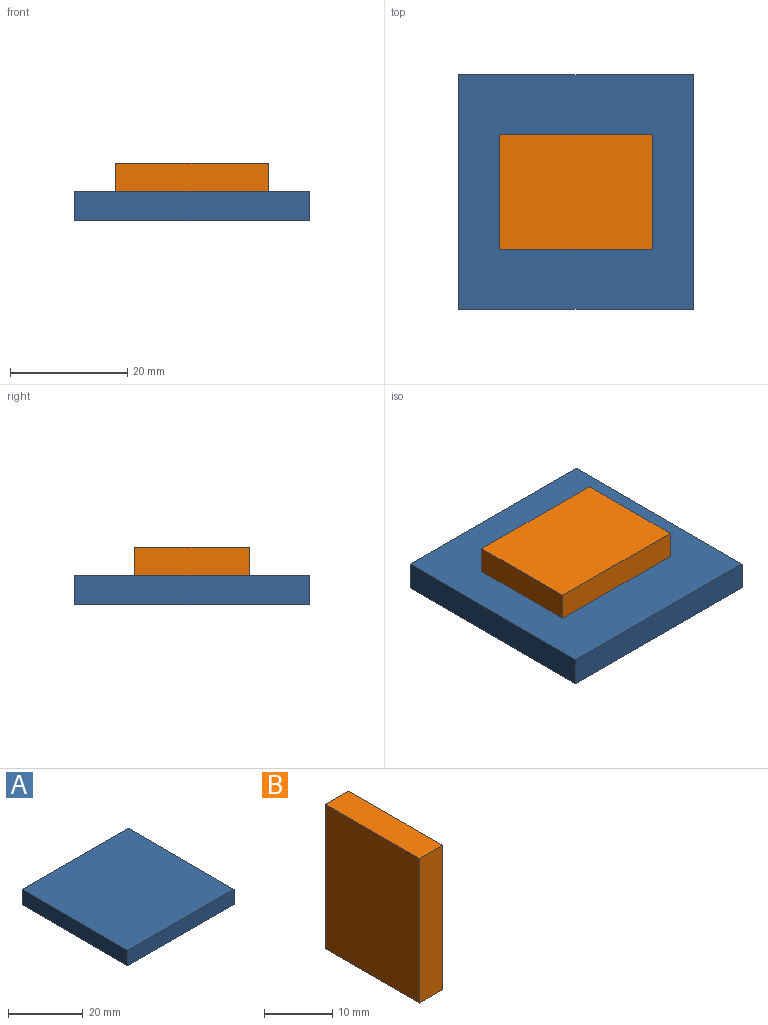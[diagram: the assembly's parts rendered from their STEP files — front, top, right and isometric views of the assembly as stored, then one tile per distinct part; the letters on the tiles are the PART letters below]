
ASSEMBLY  parts=2 mates=1
PART A: 6 faces, bbox 40x40x5 mm
  f0: plane 40x5mm, normal (0,1,0), area 200mm2, adj f1,f3,f4,f5
  f1: plane 40x5mm, normal (-1,0,0), area 200mm2, adj f0,f2,f4,f5
  f2: plane 40x5mm, normal (0,-1,0), area 200mm2, adj f1,f3,f4,f5
  f3: plane 40x5mm, normal (1,0,0), area 200mm2, adj f0,f2,f4,f5
  f4: plane 40x40mm, normal (0,0,1), area 1600mm2, adj f0,f1,f2,f3
  f5: plane 40x40mm, normal (0,0,-1), area 1600mm2, adj f0,f1,f2,f3
PART B: 6 faces, bbox 4.8x19.5x25.9 mm
  f0: plane 25.9x4.8mm, normal (0,1,0), area 124.3mm2, adj f1,f3,f4,f5
  f1: plane 19.5x4.8mm, normal (0,0,1), area 93.6mm2, adj f0,f2,f4,f5
  f2: plane 25.9x4.8mm, normal (0,-1,0), area 124.3mm2, adj f1,f3,f4,f5
  f3: plane 19.5x4.8mm, normal (0,0,-1), area 93.6mm2, adj f0,f2,f4,f5
  f4: plane 25.9x19.5mm, normal (1,0,0), area 505.1mm2, adj f0,f1,f2,f3
  f5: plane 25.9x19.5mm, normal (-1,0,0), area 505.1mm2, adj f0,f1,f2,f3
PLACE A t=(-26.43,6.75,-6.77)mm
PLACE B rot(axis=(0,1,0),90deg) t=(14.4,-61.5,3.03)mm
MATE planar A.f4 <-> B.f4  axis (0,0,1) through (-5.58,-3.53,-1.77)mm
